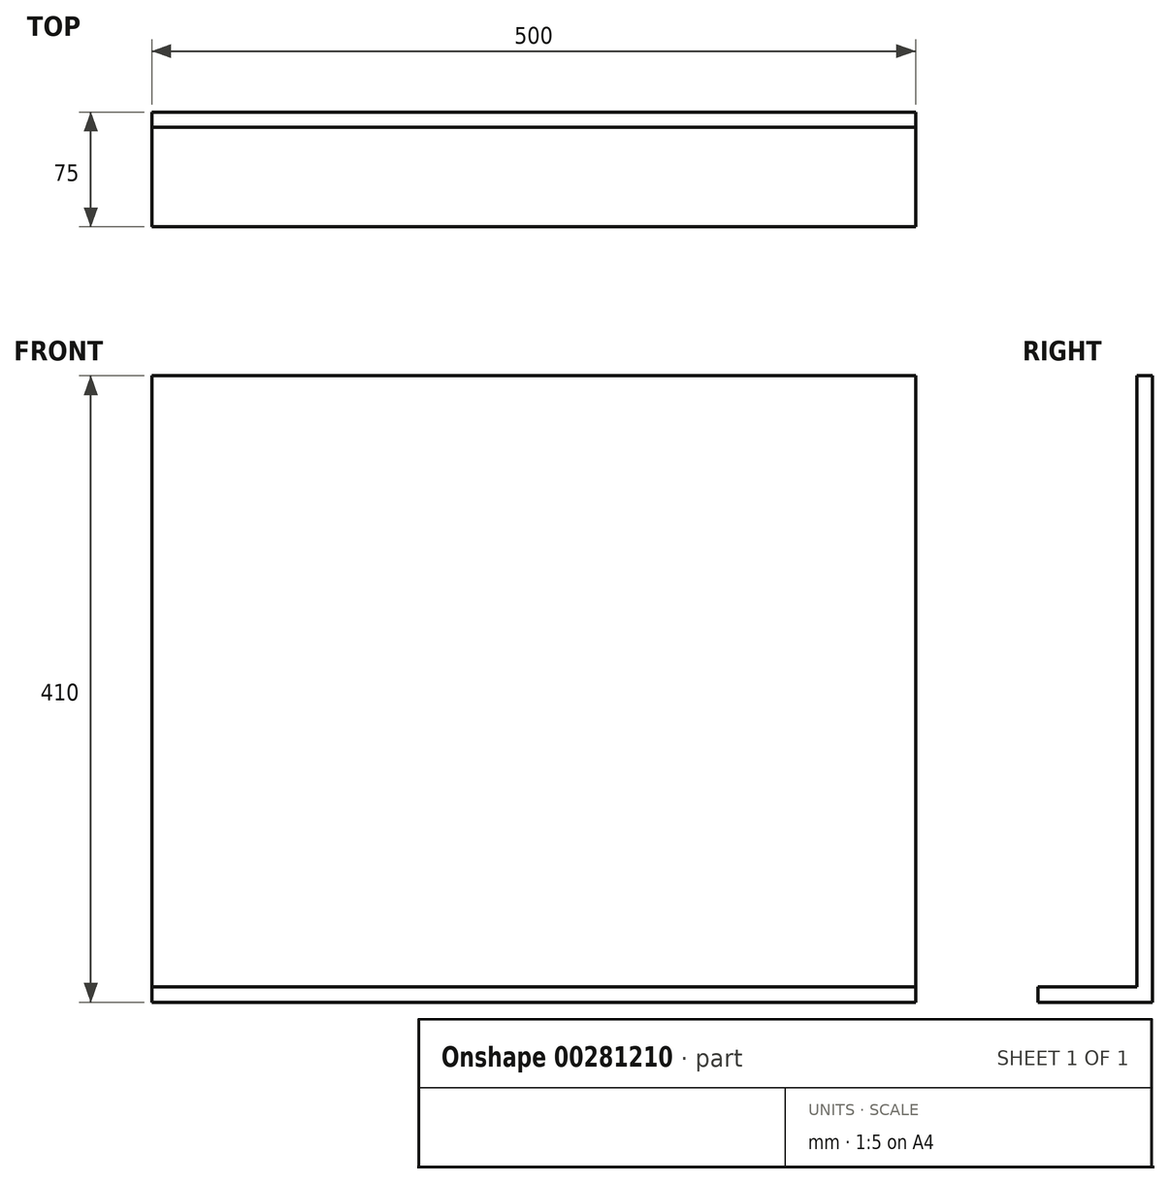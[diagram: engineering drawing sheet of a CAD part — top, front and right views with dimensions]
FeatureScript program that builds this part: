
annotation { "Feature Type Name" : "Feature", "Feature Type Description" : "" }
export const myFeature = defineFeature(function(context is Context, id is Id, definition is map)
    precondition{}
    {
        {
            var Q0;
            Q0=qCreatedBy(makeId("Right.planeOp"),FACE);
            var sketch = newSketch(context, id + "F0", { "sketchPlane" : qUnion([Q0])});
            skLineSegment(sketch, "E0", {"start": v(0, 0) * mm, "end": v(-65, 0) * mm});
            skLineSegment(sketch, "E1", {"start": v(-65, 0) * mm, "end": v(-65, -10) * mm});
            skLineSegment(sketch, "E2", {"start": v(-65, -10) * mm, "end": v(10, -10) * mm});
            skLineSegment(sketch, "E3", {"start": v(10, -10) * mm, "end": v(10, 400) * mm});
            skLineSegment(sketch, "E4", {"start": v(10, 400) * mm, "end": v(0, 400) * mm});
            skLineSegment(sketch, "E5", {"start": v(0, 400) * mm, "end": v(0, 0) * mm});
            skSolve(sketch);
        }
        {
            var Q0;
            Q0 = qSketchRegion(id + "F0", true);
            extrude(context, id + "F1", {"entities" : qUnion([Q0]), "endBound" : BoundingType.SYMMETRIC, "depth" : 500 * mm, "offsetDistance" : 25 * mm});
        }
        {
            var Q0;
            Q0=makeQuery(id+"F1.opExtrude","SWEPT_FACE",FACE,{"disambiguationData":[OSD([sQuery(id+"F0.wireOp",EDGE,"E5")])]});
            var sketch = newSketch(context, id + "F2", { "sketchPlane" : qUnion([Q0])});
            skLineSegment(sketch, "E6", {"start": v(0, 0) * mm, "end": v(0, 400) * mm, "construction": true});
            skPoint(sketch, "E7", {"position": v(0, 35) * mm});
            skPoint(sketch, "E8", {"position": v(0, 335) * mm});
            skSolve(sketch);
        }
    });
